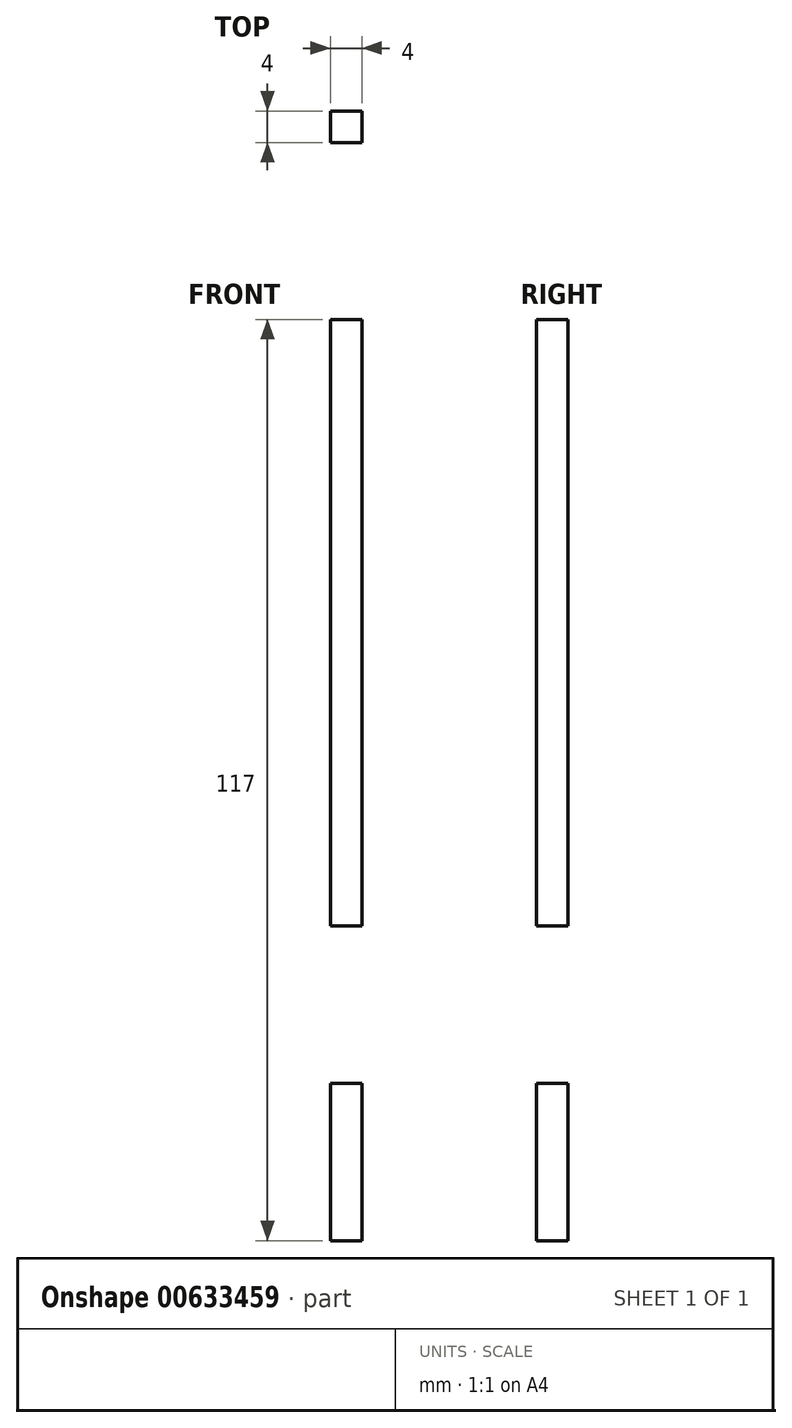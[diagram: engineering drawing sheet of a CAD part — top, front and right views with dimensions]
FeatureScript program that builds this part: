
annotation { "Feature Type Name" : "Feature", "Feature Type Description" : "" }
export const myFeature = defineFeature(function(context is Context, id is Id, definition is map)
    precondition{}
    {
        {
            var Q0;
            Q0=qCreatedBy(makeId("Front.planeOp"),FACE);
            var sketch = newSketch(context, id + "F0", { "sketchPlane" : qUnion([Q0])});
            skLineSegment(sketch, "E0.bottom", {"start": v(0, 0) * mm, "end": v(-250, 0) * mm});
            skLineSegment(sketch, "E0.left", {"start": v(0, 0) * mm, "end": v(0, 117) * mm});
            skLineSegment(sketch, "E0.right", {"start": v(-250, 0) * mm, "end": v(-250, 117) * mm});
            skLineSegment(sketch, "E1", {"start": v(-217.5, 277) * mm, "end": v(-250, 117) * mm});
            skLineSegment(sketch, "E2", {"start": v(-32.5, 277) * mm, "end": v(0, 117) * mm});
            skPoint(sketch, "E3.orphan", {"position": v(-217.5, 117) * mm});
            skLineSegment(sketch, "E4.bottom", {"start": v(-235, 277) * mm, "end": v(-217.5, 277) * mm});
            skLineSegment(sketch, "E4.top", {"start": v(-235, 362) * mm, "end": v(-15, 362) * mm});
            skLineSegment(sketch, "E4.left", {"start": v(-235, 277) * mm, "end": v(-235, 362) * mm});
            skLineSegment(sketch, "E4.right", {"start": v(-15, 277) * mm, "end": v(-15, 362) * mm});
            skLineSegment(sketch, "E5.bottom", {"start": v(-196, 0) * mm, "end": v(-146, 0) * mm});
            skLineSegment(sketch, "E5.top", {"start": v(-196, 4) * mm, "end": v(-146, 4) * mm});
            skLineSegment(sketch, "E5.left", {"start": v(-196, 0) * mm, "end": v(-196, 4) * mm});
            skLineSegment(sketch, "E5.right", {"start": v(-146, 0) * mm, "end": v(-146, 4) * mm});
            skLineSegment(sketch, "E6.bottom", {"start": v(-104, 0) * mm, "end": v(-54, 0) * mm});
            skLineSegment(sketch, "E6.top", {"start": v(-104, 4) * mm, "end": v(-54, 4) * mm});
            skLineSegment(sketch, "E6.left", {"start": v(-104, 0) * mm, "end": v(-104, 4) * mm});
            skLineSegment(sketch, "E6.right", {"start": v(-54, 0) * mm, "end": v(-54, 4) * mm});
            skLineSegment(sketch, "E7.bottom", {"start": v(-250, 117) * mm, "end": v(-246, 117) * mm});
            skLineSegment(sketch, "E7.top", {"start": v(-250, 40) * mm, "end": v(-246, 40) * mm});
            skLineSegment(sketch, "E7.left", {"start": v(-250, 117) * mm, "end": v(-250, 40) * mm});
            skLineSegment(sketch, "E7.right", {"start": v(-246, 117) * mm, "end": v(-246, 40) * mm});
            skLineSegment(sketch, "E8.bottom", {"start": v(-250, 0) * mm, "end": v(-246, 0) * mm});
            skLineSegment(sketch, "E8.top", {"start": v(-250, 20) * mm, "end": v(-246, 20) * mm});
            skLineSegment(sketch, "E8.left", {"start": v(-250, 0) * mm, "end": v(-250, 20) * mm});
            skLineSegment(sketch, "E8.right", {"start": v(-246, 0) * mm, "end": v(-246, 20) * mm});
            skLineSegment(sketch, "E9.bottom", {"start": v(0, 117) * mm, "end": v(-4, 117) * mm});
            skLineSegment(sketch, "E9.top", {"start": v(0, 40) * mm, "end": v(-4, 40) * mm});
            skLineSegment(sketch, "E9.left", {"start": v(0, 117) * mm, "end": v(0, 40) * mm});
            skLineSegment(sketch, "E9.right", {"start": v(-4, 117) * mm, "end": v(-4, 40) * mm});
            skLineSegment(sketch, "E10.bottom", {"start": v(0, 0) * mm, "end": v(-4, 0) * mm});
            skLineSegment(sketch, "E10.top", {"start": v(0, 20) * mm, "end": v(-4, 20) * mm});
            skLineSegment(sketch, "E10.left", {"start": v(0, 0) * mm, "end": v(0, 20) * mm});
            skLineSegment(sketch, "E10.right", {"start": v(-4, 0) * mm, "end": v(-4, 20) * mm});
            skLineSegment(sketch, "E11.top", {"start": v(-109.5, 273) * mm, "end": v(-69.5, 273) * mm});
            skLineSegment(sketch, "E11.left", {"start": v(-109.5, 277) * mm, "end": v(-109.5, 273) * mm});
            skLineSegment(sketch, "E11.right", {"start": v(-69.5, 277) * mm, "end": v(-69.5, 273) * mm});
            skLineSegment(sketch, "E12.bottom", {"start": v(-140.5, 277) * mm, "end": v(-180.5, 277) * mm});
            skLineSegment(sketch, "E12.top", {"start": v(-140.5, 273) * mm, "end": v(-180.5, 273) * mm});
            skLineSegment(sketch, "E12.left", {"start": v(-140.5, 277) * mm, "end": v(-140.5, 273) * mm});
            skLineSegment(sketch, "E12.right", {"start": v(-180.5, 277) * mm, "end": v(-180.5, 273) * mm});
            skLineSegment(sketch, "E13.trimOffspring", {"start": v(-109.5, 277) * mm, "end": v(-69.5, 277) * mm});
            skLineSegment(sketch, "E14.trimOffspring", {"start": v(-32.5, 277) * mm, "end": v(-15, 277) * mm});
            skLineSegment(sketch, "E15.bottom", {"start": v(-69.5, 362) * mm, "end": v(-109.5, 362) * mm});
            skLineSegment(sketch, "E15.top", {"start": v(-69.5, 358) * mm, "end": v(-109.5, 358) * mm});
            skLineSegment(sketch, "E15.left", {"start": v(-69.5, 362) * mm, "end": v(-69.5, 358) * mm});
            skLineSegment(sketch, "E15.right", {"start": v(-109.5, 362) * mm, "end": v(-109.5, 358) * mm});
            skLineSegment(sketch, "E16.bottom", {"start": v(-180.5, 362) * mm, "end": v(-140.5, 362) * mm});
            skLineSegment(sketch, "E16.top", {"start": v(-180.5, 358) * mm, "end": v(-140.5, 358) * mm});
            skLineSegment(sketch, "E16.left", {"start": v(-180.5, 362) * mm, "end": v(-180.5, 358) * mm});
            skLineSegment(sketch, "E16.right", {"start": v(-140.5, 362) * mm, "end": v(-140.5, 358) * mm});
            skSolve(sketch);
        }
        {
            var Q0;
            Q0=makeQuery(id+"F0.imprint","IMPRINT",FACE,{"disambiguationData":[TD([[makeQuery(id+"F0.imprint","IMPRINT",EDGE,{"derivedFrom":sQuery(id+"F0.wireOp",EDGE,"E0.left")}),1.0]])]});
            extrude(context, id + "F1", {"entities" : qUnion([Q0]), "depth" : 4 * mm, "offsetDistance" : 25 * mm});
        }
        {
            var Q0;
            Q0=qCreatedBy(makeId("Front.planeOp"),FACE);
            var sketch = newSketch(context, id + "F2", { "sketchPlane" : qUnion([Q0])});
            skLineSegment(sketch, "E17.bottom", {"start": v(-32.5, 345) * mm, "end": v(-34.5, 345) * mm});
            skLineSegment(sketch, "E17.top", {"start": v(-32.5, 291) * mm, "end": v(-34.5, 291) * mm});
            skLineSegment(sketch, "E17.left", {"start": v(-32.5, 345) * mm, "end": v(-32.5, 291) * mm});
            skLineSegment(sketch, "E17.right", {"start": v(-34.5, 345) * mm, "end": v(-34.5, 291) * mm});
            skLineSegment(sketch, "E18.bottom", {"start": v(-215.5, 345) * mm, "end": v(-217.5, 345) * mm});
            skLineSegment(sketch, "E18.top", {"start": v(-215.5, 291) * mm, "end": v(-217.5, 291) * mm});
            skLineSegment(sketch, "E18.left", {"start": v(-215.5, 345) * mm, "end": v(-215.5, 291) * mm});
            skLineSegment(sketch, "E18.right", {"start": v(-217.5, 345) * mm, "end": v(-217.5, 291) * mm});
            skCircle(sketch, "E19", {"center": v(-125, 289) * mm, "radius": 2 * mm});
            skLineSegment(sketch, "E20", {"start": v(-125, 362.47) * mm, "end": v(-125, 0) * mm});
            skLineSegment(sketch, "E21.bottom", {"start": v(-117.5, 39) * mm, "end": v(-132.5, 39) * mm});
            skLineSegment(sketch, "E21.top", {"start": v(-117.5, 35) * mm, "end": v(-132.5, 35) * mm});
            skLineSegment(sketch, "E21.left", {"start": v(-117.5, 39) * mm, "end": v(-117.5, 35) * mm});
            skLineSegment(sketch, "E21.right", {"start": v(-132.5, 39) * mm, "end": v(-132.5, 35) * mm});
            skLineSegment(sketch, "E22.bottom", {"start": v(-117.5, 128) * mm, "end": v(-132.5, 128) * mm});
            skLineSegment(sketch, "E22.top", {"start": v(-117.5, 124) * mm, "end": v(-132.5, 124) * mm});
            skLineSegment(sketch, "E22.left", {"start": v(-117.5, 128) * mm, "end": v(-117.5, 124) * mm});
            skLineSegment(sketch, "E22.right", {"start": v(-132.5, 128) * mm, "end": v(-132.5, 124) * mm});
            skLineSegment(sketch, "E23.bottom", {"start": v(-117.5, 217) * mm, "end": v(-132.5, 217) * mm});
            skLineSegment(sketch, "E23.top", {"start": v(-117.5, 213) * mm, "end": v(-132.5, 213) * mm});
            skLineSegment(sketch, "E23.left", {"start": v(-117.5, 217) * mm, "end": v(-117.5, 213) * mm});
            skLineSegment(sketch, "E23.right", {"start": v(-132.5, 217) * mm, "end": v(-132.5, 213) * mm});
            skSolve(sketch);
        }
        {
            var Q0;
            Q0 = qSketchRegion(id + "F2", true);
            extrude(context, id + "F3", {"entities" : qUnion([Q0]), "operationType" : NewBodyOperationType.REMOVE, "depth" : 4 * mm, "offsetDistance" : 25 * mm});
        }
    });
